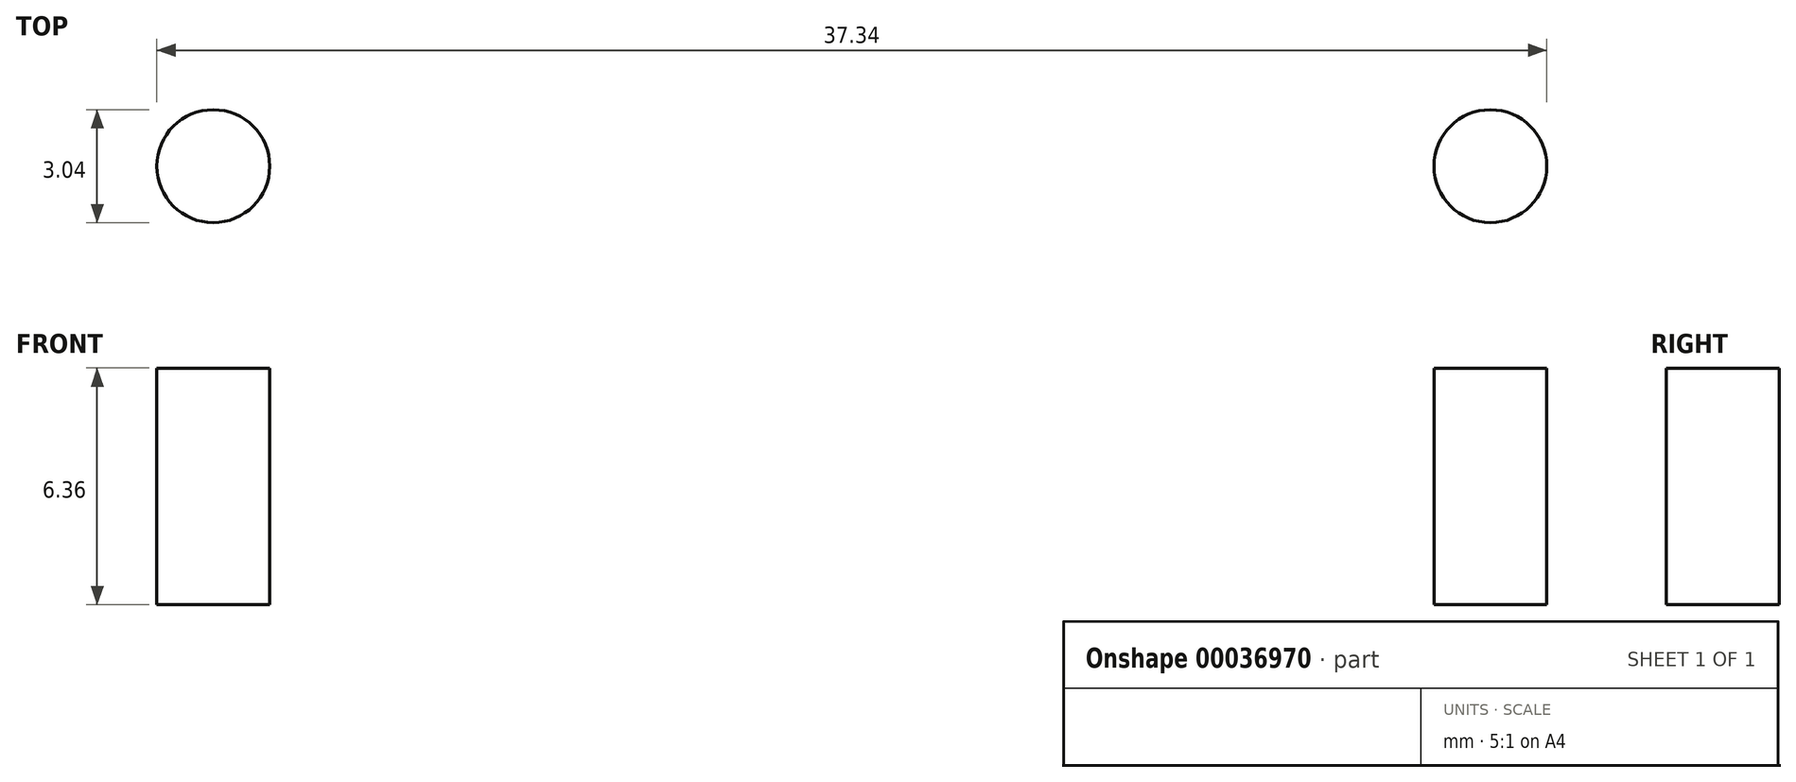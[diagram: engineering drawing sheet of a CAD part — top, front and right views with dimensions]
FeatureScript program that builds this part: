
annotation { "Feature Type Name" : "Feature", "Feature Type Description" : "" }
export const myFeature = defineFeature(function(context is Context, id is Id, definition is map)
    precondition{}
    {
        {
            var Q0;
            Q0=qCreatedBy(makeId("Right.planeOp"),FACE);
            var sketch = newSketch(context, id + "F0", { "sketchPlane" : qUnion([Q0])});
            skLineSegment(sketch, "E0.rect.bottom", {"start": v(30.48, 3.18) * mm, "end": v(-30.48, 3.18) * mm});
            skLineSegment(sketch, "E0.rect.top", {"start": v(30.48, -3.18) * mm, "end": v(-30.48, -3.18) * mm});
            skLineSegment(sketch, "E0.rect.left", {"start": v(30.48, 3.18) * mm, "end": v(30.48, -3.18) * mm});
            skLineSegment(sketch, "E0.rect.right", {"start": v(-30.48, 3.18) * mm, "end": v(-30.48, -3.18) * mm});
            skPoint(sketch, "E0.rect.middle", {"position": v(0, 0) * mm});
            skSolve(sketch);
        }
        {
            var Q0;
            Q0 = qSketchRegion(id + "F0", true);
            extrude(context, id + "F1", {"entities" : qUnion([Q0]), "endBound" : BoundingType.SYMMETRIC, "depth" : 42 * mm});
        }
        {
            var Q0;
            Q0=makeQuery(id+"F1.opExtrude","SWEPT_FACE",FACE,{"disambiguationData":[OSD([sQuery(id+"F0.wireOp",EDGE,"E0.rect.bottom")])]});
            var sketch = newSketch(context, id + "F2", { "sketchPlane" : qUnion([Q0])});
            skLineSegment(sketch, "E1", {"start": v(21, 0) * mm, "end": v(-21, 0) * mm, "construction": true});
            skLineSegment(sketch, "E2", {"start": v(-9, -26.23) * mm, "end": v(9, -26.23) * mm, "construction": true});
            skLineSegment(sketch, "E3", {"start": v(0, -30.48) * mm, "end": v(0, -26.23) * mm, "construction": true});
            skCircle(sketch, "E4", {"center": v(-9, -26.23) * mm, "radius": 1.02 * mm});
            skCircle(sketch, "E5", {"center": v(9, -26.23) * mm, "radius": 1.02 * mm});
            skCircle(sketch, "E6.MirrorC", {"center": v(9, 26.23) * mm, "radius": 1.02 * mm});
            skCircle(sketch, "E7.MirrorC", {"center": v(-9, 26.23) * mm, "radius": 1.02 * mm});
            skSolve(sketch);
        }
        {
            var Q0;
            Q0=makeQuery(id+"F1.opExtrude","SWEPT_FACE",FACE,{"disambiguationData":[OSD([sQuery(id+"F0.wireOp",EDGE,"E0.rect.bottom")])]});
            var sketch = newSketch(context, id + "F3", { "sketchPlane" : qUnion([Q0])});
            skLineSegment(sketch, "E8", {"start": v(-17.15, 26.24) * mm, "end": v(17.15, 26.24) * mm, "construction": true});
            skCircle(sketch, "E9", {"center": v(-17.15, 26.24) * mm, "radius": 1.52 * mm});
            skCircle(sketch, "E10", {"center": v(17.15, 26.24) * mm, "radius": 1.52 * mm});
            skLineSegment(sketch, "E11", {"start": v(0, 30.48) * mm, "end": v(0, 26.24) * mm, "construction": true});
            skCircle(sketch, "E12.MirrorC", {"center": v(-17.15, -26.24) * mm, "radius": 1.52 * mm});
            skCircle(sketch, "E13.MirrorC", {"center": v(17.15, -26.24) * mm, "radius": 1.52 * mm});
            skSolve(sketch);
        }
        {
            var Q0;
            Q0 = qSketchRegion(id + "F2", true);
            var Q1;
            Q1=makeQuery(id+"F3.imprint","IMPRINT",FACE,{"disambiguationData":[TD([[makeQuery(id+"F3.imprint","IMPRINT",EDGE,{"derivedFrom":sQuery(id+"F3.wireOp",EDGE,"E9")}),1.0]])]});
            var Q2;
            Q2=makeQuery(id+"F3.imprint","IMPRINT",FACE,{"disambiguationData":[TD([[makeQuery(id+"F3.imprint","IMPRINT",EDGE,{"derivedFrom":sQuery(id+"F3.wireOp",EDGE,"E10")}),1.0]])]});
            var Q3;
            Q3=makeQuery(id+"F3.imprint","IMPRINT",FACE,{"disambiguationData":[TD([[makeQuery(id+"F3.imprint","IMPRINT",EDGE,{"derivedFrom":sQuery(id+"F3.wireOp",EDGE,"E13.MirrorC")}),-1.0]])]});
            var Q4;
            Q4=makeQuery(id+"F3.imprint","IMPRINT",FACE,{"disambiguationData":[TD([[makeQuery(id+"F3.imprint","IMPRINT",EDGE,{"derivedFrom":sQuery(id+"F3.wireOp",EDGE,"E12.MirrorC")}),-1.0]])]});
            var Q5;
            Q5=makeQuery(id+"F1.opExtrude","SWEPT_FACE",FACE,{"disambiguationData":[OSD([sQuery(id+"F0.wireOp",EDGE,"E0.rect.top")])]});
            extrude(context, id + "F4", {"entities" : qUnion([Q0, Q1, Q2, Q3, Q4]), "operationType" : NewBodyOperationType.REMOVE, "endBound" : BoundingType.UP_TO_SURFACE, "oppositeDirection" : true, "endBoundEntityFace" : qUnion([Q5]), "depth" : 25.4 * mm});
        }
    });
